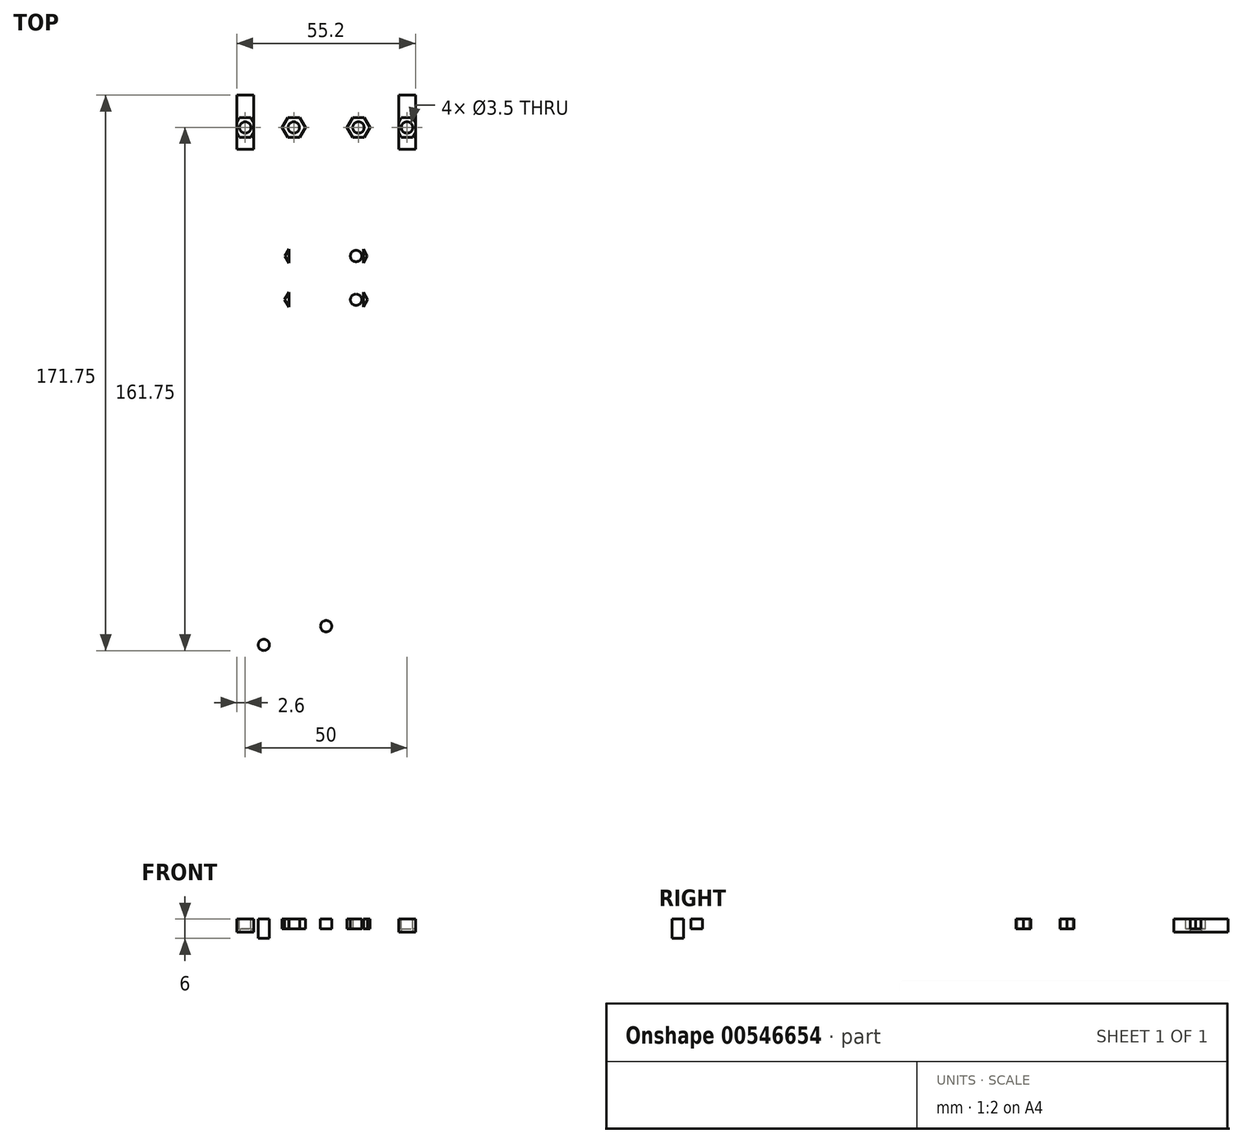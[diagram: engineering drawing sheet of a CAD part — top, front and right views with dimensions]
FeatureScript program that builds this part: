
annotation { "Feature Type Name" : "Feature", "Feature Type Description" : "" }
export const myFeature = defineFeature(function(context is Context, id is Id, definition is map)
    precondition{}
    {
        {
            var Q0;
            Q0=qCreatedBy(makeId("Top.planeOp"),FACE);
            var sketch = newSketch(context, id + "F0", { "sketchPlane" : qUnion([Q0])});
            skLineSegment(sketch, "E0.bottom", {"start": v(45, 105) * mm, "end": v(-45, 105) * mm});
            skLineSegment(sketch, "E0.top", {"start": v(45, -75) * mm, "end": v(-45, -75) * mm});
            skLineSegment(sketch, "E0.left", {"start": v(55, 95) * mm, "end": v(55, -65) * mm});
            skLineSegment(sketch, "E0.right", {"start": v(-55, 95) * mm, "end": v(-55, -65) * mm});
            skLineSegment(sketch, "E1.bottom", {"start": v(55, -3) * mm, "end": v(32, -3) * mm});
            skLineSegment(sketch, "E1.top", {"start": v(55, 77) * mm, "end": v(32, 77) * mm});
            skLineSegment(sketch, "E1.left", {"start": v(55, -3) * mm, "end": v(55, 77) * mm});
            skLineSegment(sketch, "E1.right", {"start": v(32, -3) * mm, "end": v(32, 77) * mm});
            skLineSegment(sketch, "E2.MirrorCS", {"start": v(-32, -3) * mm, "end": v(-32, 77) * mm});
            skLineSegment(sketch, "E3.MirrorCS", {"start": v(-55, 77) * mm, "end": v(-32, 77) * mm});
            skLineSegment(sketch, "E4.MirrorCS", {"start": v(-55, -3) * mm, "end": v(-55, 77) * mm});
            skLineSegment(sketch, "E5.MirrorCS", {"start": v(-55, -3) * mm, "end": v(-32, -3) * mm});
            skPoint(sketch, "E6.visualSharp", {"position": v(-55, 105) * mm});
            skArc(sketch, "E6.filletArc", {"start": v(-45, 105) * mm, "mid": v(-52.07, 102.07) * mm, "end": v(-55, 95) * mm});
            skPoint(sketch, "E7.visualSharp", {"position": v(55, 105) * mm});
            skArc(sketch, "E7.filletArc", {"start": v(55, 95) * mm, "mid": v(52.07, 102.07) * mm, "end": v(45, 105) * mm});
            skPoint(sketch, "E8.visualSharp", {"position": v(55, -75) * mm});
            skArc(sketch, "E8.filletArc", {"start": v(45, -75) * mm, "mid": v(52.07, -72.07) * mm, "end": v(55, -65) * mm});
            skPoint(sketch, "E9.visualSharp", {"position": v(-55, -75) * mm});
            skArc(sketch, "E9.filletArc", {"start": v(-55, -65) * mm, "mid": v(-52.07, -72.07) * mm, "end": v(-45, -75) * mm});
            skLineSegment(sketch, "E10.right", {"start": v(32, 28.9) * mm, "end": v(32, 75.9) * mm});
            skLineSegment(sketch, "E11.bottom", {"start": v(23, 31.6) * mm, "end": v(26, 31.6) * mm});
            skLineSegment(sketch, "E11.top", {"start": v(23, 38.2) * mm, "end": v(26, 38.2) * mm});
            skLineSegment(sketch, "E11.left", {"start": v(23, 31.6) * mm, "end": v(23, 38.2) * mm});
            skLineSegment(sketch, "E11.right", {"start": v(26, 31.6) * mm, "end": v(26, 38.2) * mm});
            skLineSegment(sketch, "E12.bottom", {"start": v(23, 66.6) * mm, "end": v(26, 66.6) * mm});
            skLineSegment(sketch, "E12.top", {"start": v(23, 73.2) * mm, "end": v(26, 73.2) * mm});
            skLineSegment(sketch, "E12.left", {"start": v(23, 66.6) * mm, "end": v(23, 73.2) * mm});
            skLineSegment(sketch, "E12.right", {"start": v(26, 66.6) * mm, "end": v(26, 73.2) * mm});
            skLineSegment(sketch, "E13.bottom", {"start": v(32, 51.9) * mm, "end": v(22, 51.9) * mm});
            skLineSegment(sketch, "E13.top", {"start": v(32, 58.9) * mm, "end": v(22, 58.9) * mm});
            skLineSegment(sketch, "E13.left", {"start": v(32, 51.9) * mm, "end": v(32, 58.9) * mm});
            skLineSegment(sketch, "E13.right", {"start": v(22, 51.9) * mm, "end": v(22, 58.9) * mm});
            skLineSegment(sketch, "E14.MirrorCS", {"start": v(-23, 73.2) * mm, "end": v(-26, 73.2) * mm});
            skLineSegment(sketch, "E15.MirrorCS", {"start": v(-26, 66.6) * mm, "end": v(-26, 73.2) * mm});
            skLineSegment(sketch, "E16.MirrorCS", {"start": v(-23, 66.6) * mm, "end": v(-23, 73.2) * mm});
            skLineSegment(sketch, "E17.MirrorCS", {"start": v(-23, 66.6) * mm, "end": v(-26, 66.6) * mm});
            skLineSegment(sketch, "E18.MirrorCS", {"start": v(-32, 51.9) * mm, "end": v(-32, 58.9) * mm});
            skLineSegment(sketch, "E19.MirrorCS", {"start": v(-32, 58.9) * mm, "end": v(-22, 58.9) * mm});
            skLineSegment(sketch, "E20.MirrorCS", {"start": v(-32, 51.9) * mm, "end": v(-22, 51.9) * mm});
            skLineSegment(sketch, "E21.MirrorCS", {"start": v(-22, 51.9) * mm, "end": v(-22, 58.9) * mm});
            skLineSegment(sketch, "E22.MirrorCS", {"start": v(-23, 38.2) * mm, "end": v(-26, 38.2) * mm});
            skLineSegment(sketch, "E23.MirrorCS", {"start": v(-23, 31.6) * mm, "end": v(-26, 31.6) * mm});
            skLineSegment(sketch, "E24.MirrorCS", {"start": v(-23, 31.6) * mm, "end": v(-23, 38.2) * mm});
            skLineSegment(sketch, "E25.MirrorCS", {"start": v(-26, 31.6) * mm, "end": v(-26, 38.2) * mm});
            skSolve(sketch);
        }
        {
            var Q0;
            Q0=makeQuery(id+"F0.imprint","IMPRINT",FACE,{"disambiguationData":[TD([[makeQuery(id+"F0.imprint","IMPRINT",EDGE,{"derivedFrom":sQuery(id+"F0.wireOp",EDGE,"E0.bottom")}),1.0]])]});
            extrude(context, id + "F1", {"entities" : qUnion([Q0]), "depth" : 6 * mm, "offsetDistance" : 25 * mm});
        }
        {
            var Q0;
            {var subQ0=sQuery(id+"F0.wireOp",EDGE,"E10.right");var subQ1=sQuery(id+"F0.wireOp",EDGE,"E1.right");var subQ2=makeQuery(id+"F0.imprint","INTERSECT",VERTEX,{"disambiguationData":[OD(0.0)],"derivedFrom":[subQ1,subQ0]});Q0=makeQuery(id+"F1.opExtrude","SWEPT_FACE",FACE,{"disambiguationData":[OSD([subQ1,subQ0]),TDD([makeQuery(id+"F0.imprint","IMPRINT",EDGE,{"disambiguationData":[TD([[makeQuery(id+"F0.imprint","INTERSECT",VERTEX,{"derivedFrom":[sQuery(id+"F0.wireOp",EDGE,"E1.bottom"),subQ1]}),-1.0]])],"derivedFrom":subQ1}),makeQuery(id+"F0.imprint","IMPRINT",EDGE,{"disambiguationData":[TD([[subQ2,-1.0]])],"derivedFrom":subQ0})])]});}
            var sketch = newSketch(context, id + "F2", { "sketchPlane" : qUnion([Q0])});
            skCircle(sketch, "E26", {"center": v(34.9, 3) * mm, "radius": 1.75 * mm});
            skCircle(sketch, "E27", {"center": v(69.9, 3) * mm, "radius": 1.75 * mm});
            skSolve(sketch);
        }
        {
            var Q0;
            Q0 = qSketchRegion(id + "F2", true);
            extrude(context, id + "F3", {"entities" : qUnion([Q0]), "operationType" : NewBodyOperationType.REMOVE, "oppositeDirection" : true, "depth" : 15 * mm, "offsetDistance" : 25 * mm});
        }
        {
            var Q0;
            {var subQ0=sQuery(id+"F0.wireOp",EDGE,"E2.MirrorCS");Q0=makeQuery(id+"F1.opExtrude","SWEPT_FACE",FACE,{"disambiguationData":[OSD([subQ0]),TDD([makeQuery(id+"F0.imprint","IMPRINT",EDGE,{"disambiguationData":[TD([[makeQuery(id+"F0.imprint","INTERSECT",VERTEX,{"derivedFrom":[subQ0,sQuery(id+"F0.wireOp",EDGE,"E3.MirrorCS")]}),1.0]])],"derivedFrom":subQ0})])]});}
            var sketch = newSketch(context, id + "F4", { "sketchPlane" : qUnion([Q0])});
            skCircle(sketch, "E28", {"center": v(-69.9, 3) * mm, "radius": 1.75 * mm});
            skCircle(sketch, "E29", {"center": v(-34.9, 3) * mm, "radius": 1.75 * mm});
            skSolve(sketch);
        }
        {
            var Q0;
            Q0=makeQuery(id+"F4.imprint","IMPRINT",FACE,{"disambiguationData":[TD([[makeQuery(id+"F4.imprint","IMPRINT",EDGE,{"derivedFrom":sQuery(id+"F4.wireOp",EDGE,"E28")}),1.0]])]});
            var Q1;
            Q1=makeQuery(id+"F4.imprint","IMPRINT",FACE,{"disambiguationData":[TD([[makeQuery(id+"F4.imprint","IMPRINT",EDGE,{"derivedFrom":sQuery(id+"F4.wireOp",EDGE,"E29")}),1.0]])]});
            extrude(context, id + "F5", {"entities" : qUnion([Q0, Q1]), "operationType" : NewBodyOperationType.REMOVE, "oppositeDirection" : true, "depth" : 15 * mm, "offsetDistance" : 25 * mm});
        }
        {
            var Q0;
            Q0=makeQuery(id+"F1.opExtrude","CAP_FACE",FACE,{"disambiguationData":[OSD([sQuery(id+"F0.wireOp",EDGE,"E0.bottom"),sQuery(id+"F0.wireOp",EDGE,"E0.top"),sQuery(id+"F0.wireOp",EDGE,"E0.left"),sQuery(id+"F0.wireOp",EDGE,"E0.right"),sQuery(id+"F0.wireOp",EDGE,"E1.bottom"),sQuery(id+"F0.wireOp",EDGE,"E1.top"),sQuery(id+"F0.wireOp",EDGE,"E1.right"),sQuery(id+"F0.wireOp",EDGE,"E2.MirrorCS"),sQuery(id+"F0.wireOp",EDGE,"E3.MirrorCS"),sQuery(id+"F0.wireOp",EDGE,"E5.MirrorCS"),sQuery(id+"F0.wireOp",EDGE,"E6.filletArc"),sQuery(id+"F0.wireOp",EDGE,"E7.filletArc"),sQuery(id+"F0.wireOp",EDGE,"E8.filletArc"),sQuery(id+"F0.wireOp",EDGE,"E9.filletArc"),sQuery(id+"F0.wireOp",EDGE,"E10.right"),sQuery(id+"F0.wireOp",EDGE,"E11.bottom"),sQuery(id+"F0.wireOp",EDGE,"E11.top"),sQuery(id+"F0.wireOp",EDGE,"E11.left"),sQuery(id+"F0.wireOp",EDGE,"E11.right"),sQuery(id+"F0.wireOp",EDGE,"E12.bottom"),sQuery(id+"F0.wireOp",EDGE,"E12.top"),sQuery(id+"F0.wireOp",EDGE,"E12.left"),sQuery(id+"F0.wireOp",EDGE,"E12.right"),sQuery(id+"F0.wireOp",EDGE,"E13.bottom"),sQuery(id+"F0.wireOp",EDGE,"E13.top"),sQuery(id+"F0.wireOp",EDGE,"E13.right"),sQuery(id+"F0.wireOp",EDGE,"E14.MirrorCS"),sQuery(id+"F0.wireOp",EDGE,"E15.MirrorCS"),sQuery(id+"F0.wireOp",EDGE,"E16.MirrorCS"),sQuery(id+"F0.wireOp",EDGE,"E17.MirrorCS"),sQuery(id+"F0.wireOp",EDGE,"E19.MirrorCS"),sQuery(id+"F0.wireOp",EDGE,"E20.MirrorCS"),sQuery(id+"F0.wireOp",EDGE,"E21.MirrorCS"),sQuery(id+"F0.wireOp",EDGE,"E22.MirrorCS"),sQuery(id+"F0.wireOp",EDGE,"E23.MirrorCS"),sQuery(id+"F0.wireOp",EDGE,"E24.MirrorCS"),sQuery(id+"F0.wireOp",EDGE,"E25.MirrorCS")])],"isStart":false});
            var sketch = newSketch(context, id + "F6", { "sketchPlane" : qUnion([Q0])});
            skLineSegment(sketch, "E30.bottom", {"start": v(11.5, 61) * mm, "end": v(-11.5, 61) * mm});
            skLineSegment(sketch, "E30.top", {"start": v(11.5, 32) * mm, "end": v(-11.5, 32) * mm});
            skLineSegment(sketch, "E30.left", {"start": v(11.5, 61) * mm, "end": v(11.5, 32) * mm});
            skLineSegment(sketch, "E30.right", {"start": v(-11.5, 61) * mm, "end": v(-11.5, 32) * mm});
            skPoint(sketch, "E30.middle", {"position": v(0, 46.5) * mm});
            skCircle(sketch, "E31", {"center": v(-9.25, 55.25) * mm, "radius": 1.75 * mm});
            skCircle(sketch, "E32.MirrorC", {"center": v(9.25, 55.25) * mm, "radius": 1.75 * mm});
            skCircle(sketch, "E33", {"center": v(-9.25, 41.75) * mm, "radius": 1.75 * mm});
            skCircle(sketch, "E34.MirrorC", {"center": v(9.25, 41.75) * mm, "radius": 1.75 * mm});
            skSolve(sketch);
        }
        {
            var Q0;
            Q0=makeQuery(id+"F6.imprint","IMPRINT",FACE,{"disambiguationData":[TD([[makeQuery(id+"F6.imprint","IMPRINT",EDGE,{"derivedFrom":sQuery(id+"F6.wireOp",EDGE,"E31")}),1.0]])]});
            var Q1;
            Q1=makeQuery(id+"F6.imprint","IMPRINT",FACE,{"disambiguationData":[TD([[makeQuery(id+"F6.imprint","IMPRINT",EDGE,{"derivedFrom":sQuery(id+"F6.wireOp",EDGE,"E32.MirrorC")}),-1.0]])]});
            var Q2;
            Q2=makeQuery(id+"F6.imprint","IMPRINT",FACE,{"disambiguationData":[TD([[makeQuery(id+"F6.imprint","IMPRINT",EDGE,{"derivedFrom":sQuery(id+"F6.wireOp",EDGE,"E34.MirrorC")}),-1.0]])]});
            var Q3;
            Q3=makeQuery(id+"F6.imprint","IMPRINT",FACE,{"disambiguationData":[TD([[makeQuery(id+"F6.imprint","IMPRINT",EDGE,{"derivedFrom":sQuery(id+"F6.wireOp",EDGE,"E33")}),1.0]])]});
            extrude(context, id + "F7", {"entities" : qUnion([Q0, Q1, Q2, Q3]), "operationType" : NewBodyOperationType.REMOVE, "oppositeDirection" : true, "depth" : 25 * mm, "offsetDistance" : 25 * mm});
        }
        {
            var Q0;
            Q0=makeQuery(id+"F1.opExtrude","CAP_FACE",FACE,{"disambiguationData":[OSD([sQuery(id+"F0.wireOp",EDGE,"E0.bottom"),sQuery(id+"F0.wireOp",EDGE,"E0.top"),sQuery(id+"F0.wireOp",EDGE,"E0.left"),sQuery(id+"F0.wireOp",EDGE,"E0.right"),sQuery(id+"F0.wireOp",EDGE,"E1.bottom"),sQuery(id+"F0.wireOp",EDGE,"E1.top"),sQuery(id+"F0.wireOp",EDGE,"E1.right"),sQuery(id+"F0.wireOp",EDGE,"E2.MirrorCS"),sQuery(id+"F0.wireOp",EDGE,"E3.MirrorCS"),sQuery(id+"F0.wireOp",EDGE,"E5.MirrorCS"),sQuery(id+"F0.wireOp",EDGE,"E6.filletArc"),sQuery(id+"F0.wireOp",EDGE,"E7.filletArc"),sQuery(id+"F0.wireOp",EDGE,"E8.filletArc"),sQuery(id+"F0.wireOp",EDGE,"E9.filletArc"),sQuery(id+"F0.wireOp",EDGE,"E10.right"),sQuery(id+"F0.wireOp",EDGE,"E11.bottom"),sQuery(id+"F0.wireOp",EDGE,"E11.top"),sQuery(id+"F0.wireOp",EDGE,"E11.left"),sQuery(id+"F0.wireOp",EDGE,"E11.right"),sQuery(id+"F0.wireOp",EDGE,"E12.bottom"),sQuery(id+"F0.wireOp",EDGE,"E12.top"),sQuery(id+"F0.wireOp",EDGE,"E12.left"),sQuery(id+"F0.wireOp",EDGE,"E12.right"),sQuery(id+"F0.wireOp",EDGE,"E13.bottom"),sQuery(id+"F0.wireOp",EDGE,"E13.top"),sQuery(id+"F0.wireOp",EDGE,"E13.right"),sQuery(id+"F0.wireOp",EDGE,"E14.MirrorCS"),sQuery(id+"F0.wireOp",EDGE,"E15.MirrorCS"),sQuery(id+"F0.wireOp",EDGE,"E16.MirrorCS"),sQuery(id+"F0.wireOp",EDGE,"E17.MirrorCS"),sQuery(id+"F0.wireOp",EDGE,"E19.MirrorCS"),sQuery(id+"F0.wireOp",EDGE,"E20.MirrorCS"),sQuery(id+"F0.wireOp",EDGE,"E21.MirrorCS"),sQuery(id+"F0.wireOp",EDGE,"E22.MirrorCS"),sQuery(id+"F0.wireOp",EDGE,"E23.MirrorCS"),sQuery(id+"F0.wireOp",EDGE,"E24.MirrorCS"),sQuery(id+"F0.wireOp",EDGE,"E25.MirrorCS")])],"isStart":true});
            var sketch = newSketch(context, id + "F8", { "sketchPlane" : qUnion([Q0])});
            skCircle(sketch, "E35.cCircle", {"center": v(-9.25, -41.75) * mm, "radius": 3.1 * mm, "construction": true});
            skLineSegment(sketch, "E35.0", {"start": v(-11.04, -38.65) * mm, "end": v(-7.46, -38.65) * mm});
            skLineSegment(sketch, "E35.1", {"start": v(-7.46, -38.65) * mm, "end": v(-5.67, -41.75) * mm});
            skLineSegment(sketch, "E35.2", {"start": v(-5.67, -41.75) * mm, "end": v(-7.46, -44.85) * mm});
            skLineSegment(sketch, "E35.3", {"start": v(-7.46, -44.85) * mm, "end": v(-11.04, -44.85) * mm});
            skLineSegment(sketch, "E35.4", {"start": v(-11.04, -44.85) * mm, "end": v(-12.83, -41.75) * mm});
            skLineSegment(sketch, "E35.5", {"start": v(-12.83, -41.75) * mm, "end": v(-11.04, -38.65) * mm});
            skPoint(sketch, "E35.0.midPoint", {"position": v(-9.25, -38.65) * mm});
            skCircle(sketch, "E36.MirrorC", {"center": v(9.25, -41.75) * mm, "radius": 3.1 * mm, "construction": true});
            skLineSegment(sketch, "E37.MirrorCS", {"start": v(5.67, -41.75) * mm, "end": v(7.46, -44.85) * mm});
            skLineSegment(sketch, "E38.MirrorCS", {"start": v(7.46, -38.65) * mm, "end": v(5.67, -41.75) * mm});
            skLineSegment(sketch, "E39.MirrorCS", {"start": v(11.04, -38.65) * mm, "end": v(7.46, -38.65) * mm});
            skPoint(sketch, "E40.MirrorP", {"position": v(9.25, -38.65) * mm});
            skLineSegment(sketch, "E41.MirrorCS", {"start": v(7.46, -44.85) * mm, "end": v(11.04, -44.85) * mm});
            skLineSegment(sketch, "E42.MirrorCS", {"start": v(11.04, -44.85) * mm, "end": v(12.83, -41.75) * mm});
            skLineSegment(sketch, "E43.MirrorCS", {"start": v(12.83, -41.75) * mm, "end": v(11.04, -38.65) * mm});
            skCircle(sketch, "E44.cCircle", {"center": v(-9.25, -55.25) * mm, "radius": 3 * mm, "construction": true});
            skLineSegment(sketch, "E44.0", {"start": v(-10.98, -52.25) * mm, "end": v(-7.52, -52.25) * mm});
            skLineSegment(sketch, "E44.1", {"start": v(-7.52, -52.25) * mm, "end": v(-5.79, -55.25) * mm});
            skLineSegment(sketch, "E44.2", {"start": v(-5.79, -55.25) * mm, "end": v(-7.52, -58.25) * mm});
            skLineSegment(sketch, "E44.3", {"start": v(-7.52, -58.25) * mm, "end": v(-10.98, -58.25) * mm});
            skLineSegment(sketch, "E44.4", {"start": v(-10.98, -58.25) * mm, "end": v(-12.71, -55.25) * mm});
            skLineSegment(sketch, "E44.5", {"start": v(-12.71, -55.25) * mm, "end": v(-10.98, -52.25) * mm});
            skPoint(sketch, "E44.0.midPoint", {"position": v(-9.25, -52.25) * mm});
            skCircle(sketch, "E45.MirrorC", {"center": v(9.25, -55.25) * mm, "radius": 3 * mm, "construction": true});
            skLineSegment(sketch, "E46.MirrorCS", {"start": v(5.79, -55.25) * mm, "end": v(7.52, -58.25) * mm});
            skLineSegment(sketch, "E47.MirrorCS", {"start": v(7.52, -52.25) * mm, "end": v(5.79, -55.25) * mm});
            skLineSegment(sketch, "E48.MirrorCS", {"start": v(10.98, -52.25) * mm, "end": v(7.52, -52.25) * mm});
            skPoint(sketch, "E49.MirrorP", {"position": v(9.25, -52.25) * mm});
            skLineSegment(sketch, "E50.MirrorCS", {"start": v(7.52, -58.25) * mm, "end": v(10.98, -58.25) * mm});
            skLineSegment(sketch, "E51.MirrorCS", {"start": v(12.71, -55.25) * mm, "end": v(10.98, -52.25) * mm});
            skLineSegment(sketch, "E52.MirrorCS", {"start": v(10.98, -58.25) * mm, "end": v(12.71, -55.25) * mm});
            skSolve(sketch);
        }
        {
            var Q0;
            Q0 = qSketchRegion(id + "F8", true);
            extrude(context, id + "F9", {"entities" : qUnion([Q0]), "operationType" : NewBodyOperationType.REMOVE, "oppositeDirection" : true, "depth" : 3 * mm, "offsetDistance" : 25 * mm});
        }
        {
            var Q0;
            Q0=makeQuery(id+"F1.opExtrude","CAP_FACE",FACE,{"disambiguationData":[OSD([sQuery(id+"F0.wireOp",EDGE,"E0.bottom"),sQuery(id+"F0.wireOp",EDGE,"E0.top"),sQuery(id+"F0.wireOp",EDGE,"E0.left"),sQuery(id+"F0.wireOp",EDGE,"E0.right"),sQuery(id+"F0.wireOp",EDGE,"E1.bottom"),sQuery(id+"F0.wireOp",EDGE,"E1.top"),sQuery(id+"F0.wireOp",EDGE,"E1.right"),sQuery(id+"F0.wireOp",EDGE,"E2.MirrorCS"),sQuery(id+"F0.wireOp",EDGE,"E3.MirrorCS"),sQuery(id+"F0.wireOp",EDGE,"E5.MirrorCS"),sQuery(id+"F0.wireOp",EDGE,"E6.filletArc"),sQuery(id+"F0.wireOp",EDGE,"E7.filletArc"),sQuery(id+"F0.wireOp",EDGE,"E8.filletArc"),sQuery(id+"F0.wireOp",EDGE,"E9.filletArc"),sQuery(id+"F0.wireOp",EDGE,"E10.right"),sQuery(id+"F0.wireOp",EDGE,"E11.bottom"),sQuery(id+"F0.wireOp",EDGE,"E11.top"),sQuery(id+"F0.wireOp",EDGE,"E11.left"),sQuery(id+"F0.wireOp",EDGE,"E11.right"),sQuery(id+"F0.wireOp",EDGE,"E12.bottom"),sQuery(id+"F0.wireOp",EDGE,"E12.top"),sQuery(id+"F0.wireOp",EDGE,"E12.left"),sQuery(id+"F0.wireOp",EDGE,"E12.right"),sQuery(id+"F0.wireOp",EDGE,"E13.bottom"),sQuery(id+"F0.wireOp",EDGE,"E13.top"),sQuery(id+"F0.wireOp",EDGE,"E13.right"),sQuery(id+"F0.wireOp",EDGE,"E14.MirrorCS"),sQuery(id+"F0.wireOp",EDGE,"E15.MirrorCS"),sQuery(id+"F0.wireOp",EDGE,"E16.MirrorCS"),sQuery(id+"F0.wireOp",EDGE,"E17.MirrorCS"),sQuery(id+"F0.wireOp",EDGE,"E19.MirrorCS"),sQuery(id+"F0.wireOp",EDGE,"E20.MirrorCS"),sQuery(id+"F0.wireOp",EDGE,"E21.MirrorCS"),sQuery(id+"F0.wireOp",EDGE,"E22.MirrorCS"),sQuery(id+"F0.wireOp",EDGE,"E23.MirrorCS"),sQuery(id+"F0.wireOp",EDGE,"E24.MirrorCS"),sQuery(id+"F0.wireOp",EDGE,"E25.MirrorCS")])],"isStart":false});
            var sketch = newSketch(context, id + "F10", { "sketchPlane" : qUnion([Q0])});
            skLineSegment(sketch, "E53.bottom", {"start": v(-55, -13) * mm, "end": v(55, -13) * mm});
            skLineSegment(sketch, "E53.top", {"start": v(-55, -55) * mm, "end": v(55, -55) * mm});
            skLineSegment(sketch, "E53.left", {"start": v(-55, -13) * mm, "end": v(-55, -55) * mm});
            skLineSegment(sketch, "E53.right", {"start": v(55, -13) * mm, "end": v(55, -55) * mm});
            skLineSegment(sketch, "E54.bottom", {"start": v(-4.2, -4.6) * mm, "end": v(4.2, -4.6) * mm});
            skLineSegment(sketch, "E54.top", {"start": v(-4.2, -13) * mm, "end": v(4.2, -13) * mm});
            skLineSegment(sketch, "E54.left", {"start": v(-4.2, -4.6) * mm, "end": v(-4.2, -13) * mm});
            skLineSegment(sketch, "E54.right", {"start": v(4.2, -4.6) * mm, "end": v(4.2, -13) * mm});
            skLineSegment(sketch, "E55.MirrorCS", {"start": v(-4.2, -55) * mm, "end": v(4.2, -55) * mm});
            skLineSegment(sketch, "E56.MirrorCS", {"start": v(-4.2, -63.4) * mm, "end": v(-4.2, -55) * mm});
            skLineSegment(sketch, "E57.MirrorCS", {"start": v(4.2, -63.4) * mm, "end": v(4.2, -55) * mm});
            skLineSegment(sketch, "E58.MirrorCS", {"start": v(-4.2, -63.4) * mm, "end": v(4.2, -63.4) * mm});
            skSolve(sketch);
        }
        {
            var Q0;
            Q0=makeQuery(id+"F10.imprint","IMPRINT",FACE,{"disambiguationData":[TD([[makeQuery(id+"F10.imprint","IMPRINT",EDGE,{"derivedFrom":sQuery(id+"F10.wireOp",EDGE,"c6e326e5-0ca1-43d0-984c-ec21a27a9c8d0.MirrorCS")}),1.0]])]});
            var Q1;
            Q1=makeQuery(id+"F10.imprint","IMPRINT",FACE,{"disambiguationData":[TD([[makeQuery(id+"F10.imprint","IMPRINT",EDGE,{"derivedFrom":sQuery(id+"F10.wireOp",EDGE,"E55.MirrorCS")}),-1.0]])]});
            var Q2;
            Q2=makeQuery(id+"F10.imprint","IMPRINT",FACE,{"disambiguationData":[TD([[makeQuery(id+"F10.imprint","IMPRINT",EDGE,{"derivedFrom":sQuery(id+"F10.wireOp",EDGE,"450c8181-7459-44c8-8380-1bca4ead6bea2.MirrorCS")}),-1.0]])]});
            var Q3;
            Q3=makeQuery(id+"F10.imprint","IMPRINT",FACE,{"disambiguationData":[TD([[makeQuery(id+"F10.imprint","IMPRINT",EDGE,{"derivedFrom":sQuery(id+"F10.wireOp",EDGE,"E54.bottom")}),-1.0]])]});
            extrude(context, id + "F11", {"entities" : qUnion([Q0, Q1, Q2, Q3]), "operationType" : NewBodyOperationType.REMOVE, "oppositeDirection" : true, "depth" : 3 * mm, "offsetDistance" : 25 * mm});
        }
        {
            var Q0;
            {var subQ2=sQuery(id+"F10.wireOp",EDGE,"E53.left");Q0=makeQuery(id+"F10.imprint","IMPRINT",FACE,{"disambiguationData":[TD([[makeQuery(id+"F10.imprint","IMPRINT",EDGE,{"derivedFrom":subQ2}),1.0]])]});}
            extrude(context, id + "F12", {"entities" : qUnion([Q0]), "operationType" : NewBodyOperationType.REMOVE, "oppositeDirection" : true, "depth" : 2 * mm, "offsetDistance" : 25 * mm});
        }
        {
            var Q0;
            Q0=makeQuery(id+"F11.boolean.opBoolean","COPY",FACE,{"derivedFrom":makeQuery(id+"F11.opExtrude","CAP_FACE",FACE,{"disambiguationData":[OSD([sQuery(id+"F10.wireOp",EDGE,"E54.bottom"),sQuery(id+"F10.wireOp",EDGE,"E54.top"),sQuery(id+"F10.wireOp",EDGE,"E54.left"),sQuery(id+"F10.wireOp",EDGE,"E54.right")])],"isStart":false})});
            var sketch = newSketch(context, id + "F13", { "sketchPlane" : qUnion([Q0])});
            skCircle(sketch, "E59", {"center": v(0, -8.8) * mm, "radius": 1.75 * mm});
            skCircle(sketch, "E60", {"center": v(0, -59.2) * mm, "radius": 1.75 * mm});
            skSolve(sketch);
        }
        {
            var Q0;
            Q0 = qSketchRegion(id + "F13", true);
            extrude(context, id + "F14", {"entities" : qUnion([Q0]), "operationType" : NewBodyOperationType.REMOVE, "oppositeDirection" : true, "depth" : 25 * mm, "offsetDistance" : 25 * mm});
        }
        {
            var Q0;
            {var subQ0=sQuery(id+"F0.wireOp",EDGE,"E12.left");var subQ1=sQuery(id+"F0.wireOp",EDGE,"E12.top");var subQ2=sQuery(id+"F0.wireOp",EDGE,"E12.bottom");var subQ3=sQuery(id+"F0.wireOp",EDGE,"E11.left");var subQ4=sQuery(id+"F0.wireOp",EDGE,"E11.top");var subQ5=sQuery(id+"F0.wireOp",EDGE,"E11.bottom");var subQ6=sQuery(id+"F0.wireOp",EDGE,"E7.filletArc");var subQ7=sQuery(id+"F0.wireOp",EDGE,"E6.filletArc");var subQ8=sQuery(id+"F0.wireOp",EDGE,"E5.MirrorCS");var subQ9=sQuery(id+"F0.wireOp",EDGE,"E3.MirrorCS");var subQ10=sQuery(id+"F0.wireOp",EDGE,"E2.MirrorCS");var subQ11=sQuery(id+"F0.wireOp",EDGE,"E19.MirrorCS");var subQ13=sQuery(id+"F0.wireOp",EDGE,"E0.right");var subQ15=sQuery(id+"F0.wireOp",EDGE,"E0.left");var subQ17=sQuery(id+"F0.wireOp",EDGE,"E1.top");var subQ18=sQuery(id+"F0.wireOp",EDGE,"E8.filletArc");var subQ19=sQuery(id+"F0.wireOp",EDGE,"E1.bottom");var subQ20=sQuery(id+"F0.wireOp",EDGE,"E11.right");var subQ21=sQuery(id+"F0.wireOp",EDGE,"E0.bottom");var subQ22=sQuery(id+"F0.wireOp",EDGE,"E10.right");var subQ23=sQuery(id+"F0.wireOp",EDGE,"E1.right");var subQ26=sQuery(id+"F0.wireOp",EDGE,"E13.top");var subQ27=sQuery(id+"F0.wireOp",EDGE,"E9.filletArc");var subQ29=sQuery(id+"F0.wireOp",EDGE,"E13.bottom");var subQ30=sQuery(id+"F0.wireOp",EDGE,"E20.MirrorCS");var subQ31=sQuery(id+"F0.wireOp",EDGE,"E12.right");var subQ32=sQuery(id+"F0.wireOp",EDGE,"E13.right");var subQ33=sQuery(id+"F0.wireOp",EDGE,"E14.MirrorCS");var subQ34=sQuery(id+"F0.wireOp",EDGE,"E15.MirrorCS");var subQ35=sQuery(id+"F0.wireOp",EDGE,"E16.MirrorCS");var subQ36=sQuery(id+"F0.wireOp",EDGE,"E17.MirrorCS");var subQ37=sQuery(id+"F0.wireOp",EDGE,"E21.MirrorCS");var subQ38=sQuery(id+"F0.wireOp",EDGE,"E22.MirrorCS");var subQ39=sQuery(id+"F0.wireOp",EDGE,"E23.MirrorCS");var subQ40=sQuery(id+"F0.wireOp",EDGE,"E24.MirrorCS");var subQ41=sQuery(id+"F0.wireOp",EDGE,"E25.MirrorCS");Q0=makeQuery(id+"F12.boolean.opBoolean","SPLIT",FACE,{"disambiguationData":[TD([makeQuery(id+"F1.opExtrude","SWEPT_FACE",FACE,{"disambiguationData":[OSD([subQ21])]})])],"derivedFrom":makeQuery(id+"F1.opExtrude","CAP_FACE",FACE,{"disambiguationData":[OSD([subQ21,sQuery(id+"F0.wireOp",EDGE,"E0.top"),subQ15,subQ13,subQ19,subQ17,subQ23,subQ10,subQ9,subQ8,subQ7,subQ6,subQ18,subQ27,subQ22,subQ5,subQ4,subQ3,subQ20,subQ2,subQ1,subQ0,subQ31,subQ29,subQ26,subQ32,subQ33,subQ34,subQ35,subQ36,subQ11,subQ30,subQ37,subQ38,subQ39,subQ40,subQ41])],"isStart":false})});}
            var sketch = newSketch(context, id + "F15", { "sketchPlane" : qUnion([Q0])});
            skCircle(sketch, "E61", {"center": v(-45, 95) * mm, "radius": 1.75 * mm});
            skCircle(sketch, "E62.MirrorC", {"center": v(45, 95) * mm, "radius": 1.75 * mm});
            skCircle(sketch, "E63", {"center": v(45, -65) * mm, "radius": 1.75 * mm});
            skCircle(sketch, "E64.MirrorC", {"center": v(-45, -65) * mm, "radius": 1.75 * mm});
            skSolve(sketch);
        }
        {
            var Q0;
            Q0 = qSketchRegion(id + "F15", true);
            extrude(context, id + "F16", {"entities" : qUnion([Q0]), "operationType" : NewBodyOperationType.REMOVE, "oppositeDirection" : true, "depth" : 25 * mm, "offsetDistance" : 25 * mm});
        }
        {
            var Q0;
            Q0=makeQuery(id+"F1.opExtrude","CAP_FACE",FACE,{"disambiguationData":[OSD([sQuery(id+"F0.wireOp",EDGE,"E0.bottom"),sQuery(id+"F0.wireOp",EDGE,"E0.top"),sQuery(id+"F0.wireOp",EDGE,"E0.left"),sQuery(id+"F0.wireOp",EDGE,"E0.right"),sQuery(id+"F0.wireOp",EDGE,"E1.bottom"),sQuery(id+"F0.wireOp",EDGE,"E1.top"),sQuery(id+"F0.wireOp",EDGE,"E1.right"),sQuery(id+"F0.wireOp",EDGE,"E2.MirrorCS"),sQuery(id+"F0.wireOp",EDGE,"E3.MirrorCS"),sQuery(id+"F0.wireOp",EDGE,"E5.MirrorCS"),sQuery(id+"F0.wireOp",EDGE,"E6.filletArc"),sQuery(id+"F0.wireOp",EDGE,"E7.filletArc"),sQuery(id+"F0.wireOp",EDGE,"E8.filletArc"),sQuery(id+"F0.wireOp",EDGE,"E9.filletArc"),sQuery(id+"F0.wireOp",EDGE,"E10.right"),sQuery(id+"F0.wireOp",EDGE,"E11.bottom"),sQuery(id+"F0.wireOp",EDGE,"E11.top"),sQuery(id+"F0.wireOp",EDGE,"E11.left"),sQuery(id+"F0.wireOp",EDGE,"E11.right"),sQuery(id+"F0.wireOp",EDGE,"E12.bottom"),sQuery(id+"F0.wireOp",EDGE,"E12.top"),sQuery(id+"F0.wireOp",EDGE,"E12.left"),sQuery(id+"F0.wireOp",EDGE,"E12.right"),sQuery(id+"F0.wireOp",EDGE,"E13.bottom"),sQuery(id+"F0.wireOp",EDGE,"E13.top"),sQuery(id+"F0.wireOp",EDGE,"E13.right"),sQuery(id+"F0.wireOp",EDGE,"E14.MirrorCS"),sQuery(id+"F0.wireOp",EDGE,"E15.MirrorCS"),sQuery(id+"F0.wireOp",EDGE,"E16.MirrorCS"),sQuery(id+"F0.wireOp",EDGE,"E17.MirrorCS"),sQuery(id+"F0.wireOp",EDGE,"E19.MirrorCS"),sQuery(id+"F0.wireOp",EDGE,"E20.MirrorCS"),sQuery(id+"F0.wireOp",EDGE,"E21.MirrorCS"),sQuery(id+"F0.wireOp",EDGE,"E22.MirrorCS"),sQuery(id+"F0.wireOp",EDGE,"E23.MirrorCS"),sQuery(id+"F0.wireOp",EDGE,"E24.MirrorCS"),sQuery(id+"F0.wireOp",EDGE,"E25.MirrorCS")])],"isStart":true});
            var sketch = newSketch(context, id + "F17", { "sketchPlane" : qUnion([Q0])});
            skCircle(sketch, "E65", {"center": v(-25, -95) * mm, "radius": 1.75 * mm});
            skCircle(sketch, "E66.MirrorC", {"center": v(25, -95) * mm, "radius": 1.75 * mm});
            skSolve(sketch);
        }
        {
            var Q0;
            Q0 = qSketchRegion(id + "F17", true);
            extrude(context, id + "F18", {"entities" : qUnion([Q0]), "operationType" : NewBodyOperationType.REMOVE, "oppositeDirection" : true, "depth" : 25 * mm, "offsetDistance" : 25 * mm});
        }
        {
            var Q0;
            {var subQ0=sQuery(id+"F0.wireOp",EDGE,"E12.left");var subQ1=sQuery(id+"F0.wireOp",EDGE,"E12.top");var subQ2=sQuery(id+"F0.wireOp",EDGE,"E12.bottom");var subQ3=sQuery(id+"F0.wireOp",EDGE,"E11.left");var subQ4=sQuery(id+"F0.wireOp",EDGE,"E11.top");var subQ5=sQuery(id+"F0.wireOp",EDGE,"E11.bottom");var subQ6=sQuery(id+"F0.wireOp",EDGE,"E7.filletArc");var subQ7=sQuery(id+"F0.wireOp",EDGE,"E6.filletArc");var subQ8=sQuery(id+"F0.wireOp",EDGE,"E5.MirrorCS");var subQ9=sQuery(id+"F0.wireOp",EDGE,"E3.MirrorCS");var subQ10=sQuery(id+"F0.wireOp",EDGE,"E2.MirrorCS");var subQ11=sQuery(id+"F0.wireOp",EDGE,"E19.MirrorCS");var subQ13=sQuery(id+"F0.wireOp",EDGE,"E0.right");var subQ15=sQuery(id+"F0.wireOp",EDGE,"E0.left");var subQ17=sQuery(id+"F0.wireOp",EDGE,"E1.top");var subQ18=sQuery(id+"F0.wireOp",EDGE,"E8.filletArc");var subQ19=sQuery(id+"F0.wireOp",EDGE,"E1.bottom");var subQ20=sQuery(id+"F0.wireOp",EDGE,"E11.right");var subQ21=sQuery(id+"F0.wireOp",EDGE,"E0.bottom");var subQ22=sQuery(id+"F0.wireOp",EDGE,"E10.right");var subQ23=sQuery(id+"F0.wireOp",EDGE,"E1.right");var subQ26=sQuery(id+"F0.wireOp",EDGE,"E13.top");var subQ27=sQuery(id+"F0.wireOp",EDGE,"E9.filletArc");var subQ29=sQuery(id+"F0.wireOp",EDGE,"E13.bottom");var subQ30=sQuery(id+"F0.wireOp",EDGE,"E20.MirrorCS");var subQ31=sQuery(id+"F0.wireOp",EDGE,"E12.right");var subQ32=sQuery(id+"F0.wireOp",EDGE,"E13.right");var subQ33=sQuery(id+"F0.wireOp",EDGE,"E14.MirrorCS");var subQ34=sQuery(id+"F0.wireOp",EDGE,"E15.MirrorCS");var subQ35=sQuery(id+"F0.wireOp",EDGE,"E16.MirrorCS");var subQ36=sQuery(id+"F0.wireOp",EDGE,"E17.MirrorCS");var subQ37=sQuery(id+"F0.wireOp",EDGE,"E21.MirrorCS");var subQ38=sQuery(id+"F0.wireOp",EDGE,"E22.MirrorCS");var subQ39=sQuery(id+"F0.wireOp",EDGE,"E23.MirrorCS");var subQ40=sQuery(id+"F0.wireOp",EDGE,"E24.MirrorCS");var subQ41=sQuery(id+"F0.wireOp",EDGE,"E25.MirrorCS");Q0=makeQuery(id+"F12.boolean.opBoolean","SPLIT",FACE,{"disambiguationData":[TD([makeQuery(id+"F1.opExtrude","SWEPT_FACE",FACE,{"disambiguationData":[OSD([subQ21])]})])],"derivedFrom":makeQuery(id+"F1.opExtrude","CAP_FACE",FACE,{"disambiguationData":[OSD([subQ21,sQuery(id+"F0.wireOp",EDGE,"E0.top"),subQ15,subQ13,subQ19,subQ17,subQ23,subQ10,subQ9,subQ8,subQ7,subQ6,subQ18,subQ27,subQ22,subQ5,subQ4,subQ3,subQ20,subQ2,subQ1,subQ0,subQ31,subQ29,subQ26,subQ32,subQ33,subQ34,subQ35,subQ36,subQ11,subQ30,subQ37,subQ38,subQ39,subQ40,subQ41])],"isStart":false})});}
            var sketch = newSketch(context, id + "F19", { "sketchPlane" : qUnion([Q0])});
            skCircle(sketch, "E67.cCircle", {"center": v(-25, 95) * mm, "radius": 3.1 * mm, "construction": true});
            skLineSegment(sketch, "E67.0", {"start": v(-26.79, 98.1) * mm, "end": v(-23.21, 98.1) * mm});
            skLineSegment(sketch, "E67.1", {"start": v(-23.21, 98.1) * mm, "end": v(-21.42, 95) * mm});
            skLineSegment(sketch, "E67.2", {"start": v(-21.42, 95) * mm, "end": v(-23.21, 91.9) * mm});
            skLineSegment(sketch, "E67.3", {"start": v(-23.21, 91.9) * mm, "end": v(-26.79, 91.9) * mm});
            skLineSegment(sketch, "E67.4", {"start": v(-26.79, 91.9) * mm, "end": v(-28.58, 95) * mm});
            skLineSegment(sketch, "E67.5", {"start": v(-28.58, 95) * mm, "end": v(-26.79, 98.1) * mm});
            skPoint(sketch, "E67.0.midPoint", {"position": v(-25, 98.1) * mm});
            skLineSegment(sketch, "E68.MirrorCS", {"start": v(26.79, 91.9) * mm, "end": v(28.58, 95) * mm});
            skLineSegment(sketch, "E69.MirrorCS", {"start": v(23.21, 98.1) * mm, "end": v(21.42, 95) * mm});
            skLineSegment(sketch, "E70.MirrorCS", {"start": v(23.21, 91.9) * mm, "end": v(26.79, 91.9) * mm});
            skPoint(sketch, "E71.MirrorP", {"position": v(25, 98.1) * mm});
            skLineSegment(sketch, "E72.MirrorCS", {"start": v(21.42, 95) * mm, "end": v(23.21, 91.9) * mm});
            skLineSegment(sketch, "E73.MirrorCS", {"start": v(26.79, 98.1) * mm, "end": v(23.21, 98.1) * mm});
            skCircle(sketch, "E74.MirrorC", {"center": v(25, 95) * mm, "radius": 3.1 * mm, "construction": true});
            skLineSegment(sketch, "E75.MirrorCS", {"start": v(28.58, 95) * mm, "end": v(26.79, 98.1) * mm});
            skSolve(sketch);
        }
        {
            var Q0;
            Q0 = qSketchRegion(id + "F19", true);
            extrude(context, id + "F20", {"entities" : qUnion([Q0]), "operationType" : NewBodyOperationType.REMOVE, "oppositeDirection" : true, "depth" : 3 * mm, "offsetDistance" : 25 * mm});
        }
        {
            var Q0;
            Q0=makeQuery(id+"F1.opExtrude","CAP_FACE",FACE,{"disambiguationData":[OSD([sQuery(id+"F0.wireOp",EDGE,"E0.bottom"),sQuery(id+"F0.wireOp",EDGE,"E0.top"),sQuery(id+"F0.wireOp",EDGE,"E0.left"),sQuery(id+"F0.wireOp",EDGE,"E0.right"),sQuery(id+"F0.wireOp",EDGE,"E1.bottom"),sQuery(id+"F0.wireOp",EDGE,"E1.top"),sQuery(id+"F0.wireOp",EDGE,"E1.right"),sQuery(id+"F0.wireOp",EDGE,"E2.MirrorCS"),sQuery(id+"F0.wireOp",EDGE,"E3.MirrorCS"),sQuery(id+"F0.wireOp",EDGE,"E5.MirrorCS"),sQuery(id+"F0.wireOp",EDGE,"E6.filletArc"),sQuery(id+"F0.wireOp",EDGE,"E7.filletArc"),sQuery(id+"F0.wireOp",EDGE,"E8.filletArc"),sQuery(id+"F0.wireOp",EDGE,"E9.filletArc"),sQuery(id+"F0.wireOp",EDGE,"E10.right"),sQuery(id+"F0.wireOp",EDGE,"E11.bottom"),sQuery(id+"F0.wireOp",EDGE,"E11.top"),sQuery(id+"F0.wireOp",EDGE,"E11.left"),sQuery(id+"F0.wireOp",EDGE,"E11.right"),sQuery(id+"F0.wireOp",EDGE,"E12.bottom"),sQuery(id+"F0.wireOp",EDGE,"E12.top"),sQuery(id+"F0.wireOp",EDGE,"E12.left"),sQuery(id+"F0.wireOp",EDGE,"E12.right"),sQuery(id+"F0.wireOp",EDGE,"E13.bottom"),sQuery(id+"F0.wireOp",EDGE,"E13.top"),sQuery(id+"F0.wireOp",EDGE,"E13.right"),sQuery(id+"F0.wireOp",EDGE,"E14.MirrorCS"),sQuery(id+"F0.wireOp",EDGE,"E15.MirrorCS"),sQuery(id+"F0.wireOp",EDGE,"E16.MirrorCS"),sQuery(id+"F0.wireOp",EDGE,"E17.MirrorCS"),sQuery(id+"F0.wireOp",EDGE,"E19.MirrorCS"),sQuery(id+"F0.wireOp",EDGE,"E20.MirrorCS"),sQuery(id+"F0.wireOp",EDGE,"E21.MirrorCS"),sQuery(id+"F0.wireOp",EDGE,"E22.MirrorCS"),sQuery(id+"F0.wireOp",EDGE,"E23.MirrorCS"),sQuery(id+"F0.wireOp",EDGE,"E24.MirrorCS"),sQuery(id+"F0.wireOp",EDGE,"E25.MirrorCS")])],"isStart":true});
            var sketch = newSketch(context, id + "F21", { "sketchPlane" : qUnion([Q0])});
            skCircle(sketch, "E76", {"center": v(-10, -95) * mm, "radius": 1.75 * mm});
            skCircle(sketch, "E77.MirrorC", {"center": v(10, -95) * mm, "radius": 1.75 * mm});
            skSolve(sketch);
        }
        {
            var Q0;
            Q0 = qSketchRegion(id + "F21", true);
            extrude(context, id + "F22", {"entities" : qUnion([Q0]), "operationType" : NewBodyOperationType.REMOVE, "oppositeDirection" : true, "depth" : 25 * mm, "offsetDistance" : 25 * mm});
        }
        {
            var Q0;
            Q0=makeQuery(id+"F1.opExtrude","CAP_FACE",FACE,{"disambiguationData":[OSD([sQuery(id+"F0.wireOp",EDGE,"E0.bottom"),sQuery(id+"F0.wireOp",EDGE,"E0.top"),sQuery(id+"F0.wireOp",EDGE,"E0.left"),sQuery(id+"F0.wireOp",EDGE,"E0.right"),sQuery(id+"F0.wireOp",EDGE,"E1.bottom"),sQuery(id+"F0.wireOp",EDGE,"E1.top"),sQuery(id+"F0.wireOp",EDGE,"E1.right"),sQuery(id+"F0.wireOp",EDGE,"E2.MirrorCS"),sQuery(id+"F0.wireOp",EDGE,"E3.MirrorCS"),sQuery(id+"F0.wireOp",EDGE,"E5.MirrorCS"),sQuery(id+"F0.wireOp",EDGE,"E6.filletArc"),sQuery(id+"F0.wireOp",EDGE,"E7.filletArc"),sQuery(id+"F0.wireOp",EDGE,"E8.filletArc"),sQuery(id+"F0.wireOp",EDGE,"E9.filletArc"),sQuery(id+"F0.wireOp",EDGE,"E10.right"),sQuery(id+"F0.wireOp",EDGE,"E11.bottom"),sQuery(id+"F0.wireOp",EDGE,"E11.top"),sQuery(id+"F0.wireOp",EDGE,"E11.left"),sQuery(id+"F0.wireOp",EDGE,"E11.right"),sQuery(id+"F0.wireOp",EDGE,"E12.bottom"),sQuery(id+"F0.wireOp",EDGE,"E12.top"),sQuery(id+"F0.wireOp",EDGE,"E12.left"),sQuery(id+"F0.wireOp",EDGE,"E12.right"),sQuery(id+"F0.wireOp",EDGE,"E13.bottom"),sQuery(id+"F0.wireOp",EDGE,"E13.top"),sQuery(id+"F0.wireOp",EDGE,"E13.right"),sQuery(id+"F0.wireOp",EDGE,"E14.MirrorCS"),sQuery(id+"F0.wireOp",EDGE,"E15.MirrorCS"),sQuery(id+"F0.wireOp",EDGE,"E16.MirrorCS"),sQuery(id+"F0.wireOp",EDGE,"E17.MirrorCS"),sQuery(id+"F0.wireOp",EDGE,"E19.MirrorCS"),sQuery(id+"F0.wireOp",EDGE,"E20.MirrorCS"),sQuery(id+"F0.wireOp",EDGE,"E21.MirrorCS"),sQuery(id+"F0.wireOp",EDGE,"E22.MirrorCS"),sQuery(id+"F0.wireOp",EDGE,"E23.MirrorCS"),sQuery(id+"F0.wireOp",EDGE,"E24.MirrorCS"),sQuery(id+"F0.wireOp",EDGE,"E25.MirrorCS")])],"isStart":true});
            var sketch = newSketch(context, id + "F23", { "sketchPlane" : qUnion([Q0])});
            skCircle(sketch, "E78.cCircle", {"center": v(-10, -95) * mm, "radius": 3.1 * mm, "construction": true});
            skLineSegment(sketch, "E78.0", {"start": v(-11.79, -91.9) * mm, "end": v(-8.21, -91.9) * mm});
            skLineSegment(sketch, "E78.1", {"start": v(-8.21, -91.9) * mm, "end": v(-6.42, -95) * mm});
            skLineSegment(sketch, "E78.2", {"start": v(-6.42, -95) * mm, "end": v(-8.21, -98.1) * mm});
            skLineSegment(sketch, "E78.3", {"start": v(-8.21, -98.1) * mm, "end": v(-11.79, -98.1) * mm});
            skLineSegment(sketch, "E78.4", {"start": v(-11.79, -98.1) * mm, "end": v(-13.58, -95) * mm});
            skLineSegment(sketch, "E78.5", {"start": v(-13.58, -95) * mm, "end": v(-11.79, -91.9) * mm});
            skPoint(sketch, "E78.0.midPoint", {"position": v(-10, -91.9) * mm});
            skLineSegment(sketch, "E79.MirrorCS", {"start": v(11.79, -91.9) * mm, "end": v(8.21, -91.9) * mm});
            skLineSegment(sketch, "E80.MirrorCS", {"start": v(8.21, -91.9) * mm, "end": v(6.42, -95) * mm});
            skPoint(sketch, "E81.MirrorP", {"position": v(10, -91.9) * mm});
            skLineSegment(sketch, "E82.MirrorCS", {"start": v(6.42, -95) * mm, "end": v(8.21, -98.1) * mm});
            skLineSegment(sketch, "E83.MirrorCS", {"start": v(8.21, -98.1) * mm, "end": v(11.79, -98.1) * mm});
            skCircle(sketch, "E84.MirrorC", {"center": v(10, -95) * mm, "radius": 3.1 * mm, "construction": true});
            skLineSegment(sketch, "E85.MirrorCS", {"start": v(11.79, -98.1) * mm, "end": v(13.58, -95) * mm});
            skLineSegment(sketch, "E86.MirrorCS", {"start": v(13.58, -95) * mm, "end": v(11.79, -91.9) * mm});
            skSolve(sketch);
        }
        {
            var Q0;
            Q0 = qSketchRegion(id + "F23", true);
            extrude(context, id + "F24", {"entities" : qUnion([Q0]), "operationType" : NewBodyOperationType.REMOVE, "oppositeDirection" : true, "depth" : 3 * mm, "offsetDistance" : 25 * mm});
        }
        {
            var Q0;
            {var subQ0=sQuery(id+"F0.wireOp",EDGE,"E12.left");var subQ1=sQuery(id+"F0.wireOp",EDGE,"E12.top");var subQ2=sQuery(id+"F0.wireOp",EDGE,"E12.bottom");var subQ3=sQuery(id+"F0.wireOp",EDGE,"E11.left");var subQ4=sQuery(id+"F0.wireOp",EDGE,"E11.top");var subQ5=sQuery(id+"F0.wireOp",EDGE,"E11.bottom");var subQ6=sQuery(id+"F0.wireOp",EDGE,"E7.filletArc");var subQ7=sQuery(id+"F0.wireOp",EDGE,"E6.filletArc");var subQ8=sQuery(id+"F0.wireOp",EDGE,"E5.MirrorCS");var subQ9=sQuery(id+"F0.wireOp",EDGE,"E3.MirrorCS");var subQ10=sQuery(id+"F0.wireOp",EDGE,"E2.MirrorCS");var subQ11=sQuery(id+"F0.wireOp",EDGE,"E19.MirrorCS");var subQ13=sQuery(id+"F0.wireOp",EDGE,"E0.right");var subQ15=sQuery(id+"F0.wireOp",EDGE,"E0.left");var subQ17=sQuery(id+"F0.wireOp",EDGE,"E1.top");var subQ18=sQuery(id+"F0.wireOp",EDGE,"E8.filletArc");var subQ19=sQuery(id+"F0.wireOp",EDGE,"E1.bottom");var subQ20=sQuery(id+"F0.wireOp",EDGE,"E11.right");var subQ21=sQuery(id+"F0.wireOp",EDGE,"E0.bottom");var subQ22=sQuery(id+"F0.wireOp",EDGE,"E10.right");var subQ23=sQuery(id+"F0.wireOp",EDGE,"E1.right");var subQ26=sQuery(id+"F0.wireOp",EDGE,"E13.top");var subQ27=sQuery(id+"F0.wireOp",EDGE,"E9.filletArc");var subQ29=sQuery(id+"F0.wireOp",EDGE,"E13.bottom");var subQ30=sQuery(id+"F0.wireOp",EDGE,"E20.MirrorCS");var subQ31=sQuery(id+"F0.wireOp",EDGE,"E12.right");var subQ32=sQuery(id+"F0.wireOp",EDGE,"E13.right");var subQ33=sQuery(id+"F0.wireOp",EDGE,"E14.MirrorCS");var subQ34=sQuery(id+"F0.wireOp",EDGE,"E15.MirrorCS");var subQ35=sQuery(id+"F0.wireOp",EDGE,"E16.MirrorCS");var subQ36=sQuery(id+"F0.wireOp",EDGE,"E17.MirrorCS");var subQ37=sQuery(id+"F0.wireOp",EDGE,"E21.MirrorCS");var subQ38=sQuery(id+"F0.wireOp",EDGE,"E22.MirrorCS");var subQ39=sQuery(id+"F0.wireOp",EDGE,"E23.MirrorCS");var subQ40=sQuery(id+"F0.wireOp",EDGE,"E24.MirrorCS");var subQ41=sQuery(id+"F0.wireOp",EDGE,"E25.MirrorCS");Q0=makeQuery(id+"F12.boolean.opBoolean","SPLIT",FACE,{"disambiguationData":[TD([makeQuery(id+"F1.opExtrude","SWEPT_FACE",FACE,{"disambiguationData":[OSD([subQ21])]})])],"derivedFrom":makeQuery(id+"F1.opExtrude","CAP_FACE",FACE,{"disambiguationData":[OSD([subQ21,sQuery(id+"F0.wireOp",EDGE,"E0.top"),subQ15,subQ13,subQ19,subQ17,subQ23,subQ10,subQ9,subQ8,subQ7,subQ6,subQ18,subQ27,subQ22,subQ5,subQ4,subQ3,subQ20,subQ2,subQ1,subQ0,subQ31,subQ29,subQ26,subQ32,subQ33,subQ34,subQ35,subQ36,subQ11,subQ30,subQ37,subQ38,subQ39,subQ40,subQ41])],"isStart":false})});}
            var sketch = newSketch(context, id + "F25", { "sketchPlane" : qUnion([Q0])});
            skLineSegment(sketch, "E87.bottom", {"start": v(15, 30) * mm, "end": v(-15, 30) * mm});
            skLineSegment(sketch, "E87.top", {"start": v(15, 0) * mm, "end": v(-15, 0) * mm});
            skLineSegment(sketch, "E87.left", {"start": v(15, 30) * mm, "end": v(15, 0) * mm});
            skLineSegment(sketch, "E87.right", {"start": v(-15, 30) * mm, "end": v(-15, 0) * mm});
            skPoint(sketch, "E87.middle", {"position": v(0, 15) * mm});
            skLineSegment(sketch, "E88", {"start": v(-12.5, 0) * mm, "end": v(15, 27.5) * mm});
            skLineSegment(sketch, "E89", {"start": v(-15, 2.5) * mm, "end": v(12.5, 30) * mm});
            skLineSegment(sketch, "E90", {"start": v(-15, 27.5) * mm, "end": v(12.5, 0) * mm});
            skLineSegment(sketch, "E91", {"start": v(-12.5, 30) * mm, "end": v(15, 2.5) * mm});
            skSolve(sketch);
        }
        {
            var Q0;
            {var subQ0=sQuery(id+"F25.wireOp",EDGE,"E89");var subQ1=sQuery(id+"F25.wireOp",EDGE,"E87.bottom");var subQ2=makeQuery(id+"F25.imprint","INTERSECT",VERTEX,{"derivedFrom":[subQ1,subQ0]});Q0=makeQuery(id+"F25.imprint","IMPRINT",FACE,{"disambiguationData":[TD([[makeQuery(id+"F25.imprint","IMPRINT",EDGE,{"disambiguationData":[TD([[subQ2,-1.0]])],"derivedFrom":subQ1}),1.0]])]});}
            var Q1;
            {var subQ0=sQuery(id+"F25.wireOp",EDGE,"E89");var subQ1=sQuery(id+"F25.wireOp",EDGE,"E87.right");var subQ2=makeQuery(id+"F25.imprint","INTERSECT",VERTEX,{"derivedFrom":[subQ1,subQ0]});Q1=makeQuery(id+"F25.imprint","IMPRINT",FACE,{"disambiguationData":[TD([[makeQuery(id+"F25.imprint","IMPRINT",EDGE,{"disambiguationData":[TD([[subQ2,1.0]])],"derivedFrom":subQ1}),1.0]])]});}
            var Q2;
            {var subQ0=sQuery(id+"F25.wireOp",EDGE,"E88");var subQ1=sQuery(id+"F25.wireOp",EDGE,"E87.top");var subQ2=makeQuery(id+"F25.imprint","INTERSECT",VERTEX,{"derivedFrom":[subQ1,subQ0]});Q2=makeQuery(id+"F25.imprint","IMPRINT",FACE,{"disambiguationData":[TD([[makeQuery(id+"F25.imprint","IMPRINT",EDGE,{"disambiguationData":[TD([[subQ2,1.0]])],"derivedFrom":subQ1}),-1.0]])]});}
            var Q3;
            {var subQ0=sQuery(id+"F25.wireOp",EDGE,"E88");var subQ1=sQuery(id+"F25.wireOp",EDGE,"E87.left");var subQ2=makeQuery(id+"F25.imprint","INTERSECT",VERTEX,{"derivedFrom":[subQ1,subQ0]});Q3=makeQuery(id+"F25.imprint","IMPRINT",FACE,{"disambiguationData":[TD([[makeQuery(id+"F25.imprint","IMPRINT",EDGE,{"disambiguationData":[TD([[subQ2,-1.0]])],"derivedFrom":subQ1}),-1.0]])]});}
            extrude(context, id + "F26", {"entities" : qUnion([Q0, Q1, Q2, Q3]), "operationType" : NewBodyOperationType.REMOVE, "oppositeDirection" : true, "depth" : 25 * mm, "offsetDistance" : 25 * mm});
        }
        {
            var Q0;
            Q0=makeQuery(id+"F12.boolean.opBoolean","COPY",FACE,{"derivedFrom":makeQuery(id+"F12.opExtrude","CAP_FACE",FACE,{"disambiguationData":[OSD([sQuery(id+"F10.wireOp",EDGE,"E53.bottom"),sQuery(id+"F10.wireOp",EDGE,"E53.top"),sQuery(id+"F10.wireOp",EDGE,"E53.left"),sQuery(id+"F10.wireOp",EDGE,"E53.right"),sQuery(id+"F10.wireOp",EDGE,"E54.top"),sQuery(id+"F10.wireOp",EDGE,"E55.MirrorCS")])],"isStart":false})});
            var sketch = newSketch(context, id + "F27", { "sketchPlane" : qUnion([Q0])});
            skLineSegment(sketch, "E92.bottom", {"start": v(-42.5, -46.5) * mm, "end": v(-17.5, -46.5) * mm});
            skLineSegment(sketch, "E92.top", {"start": v(-42.5, -21.5) * mm, "end": v(-17.5, -21.5) * mm});
            skLineSegment(sketch, "E92.left", {"start": v(-42.5, -46.5) * mm, "end": v(-42.5, -21.5) * mm});
            skLineSegment(sketch, "E92.right", {"start": v(-17.5, -46.5) * mm, "end": v(-17.5, -21.5) * mm});
            skLineSegment(sketch, "E93", {"start": v(-42.5, -24) * mm, "end": v(-20, -46.5) * mm});
            skLineSegment(sketch, "E94", {"start": v(-40, -21.5) * mm, "end": v(-17.5, -44) * mm});
            skLineSegment(sketch, "E95", {"start": v(-42.5, -44) * mm, "end": v(-20, -21.5) * mm});
            skLineSegment(sketch, "E96", {"start": v(-40, -46.5) * mm, "end": v(-17.5, -24) * mm});
            skLineSegment(sketch, "E97.1.0.0", {"start": v(-10, -21.5) * mm, "end": v(12.5, -44) * mm});
            skLineSegment(sketch, "E97.1.0.1", {"start": v(-12.5, -44) * mm, "end": v(10, -21.5) * mm});
            skLineSegment(sketch, "E97.1.0.2", {"start": v(12.5, -46.5) * mm, "end": v(12.5, -21.5) * mm});
            skLineSegment(sketch, "E97.1.0.3", {"start": v(-12.5, -24) * mm, "end": v(10, -46.5) * mm});
            skLineSegment(sketch, "E97.1.0.4", {"start": v(-12.5, -46.5) * mm, "end": v(12.5, -46.5) * mm});
            skLineSegment(sketch, "E97.1.0.5", {"start": v(-10, -46.5) * mm, "end": v(12.5, -24) * mm});
            skLineSegment(sketch, "E97.1.0.6", {"start": v(-12.5, -21.5) * mm, "end": v(12.5, -21.5) * mm});
            skLineSegment(sketch, "E97.1.0.7", {"start": v(-12.5, -46.5) * mm, "end": v(-12.5, -21.5) * mm});
            skLineSegment(sketch, "E97.2.0.0", {"start": v(20, -21.5) * mm, "end": v(42.5, -44) * mm});
            skLineSegment(sketch, "E97.2.0.1", {"start": v(17.5, -44) * mm, "end": v(40, -21.5) * mm});
            skLineSegment(sketch, "E97.2.0.2", {"start": v(42.5, -46.5) * mm, "end": v(42.5, -21.5) * mm});
            skLineSegment(sketch, "E97.2.0.3", {"start": v(17.5, -24) * mm, "end": v(40, -46.5) * mm});
            skLineSegment(sketch, "E97.2.0.4", {"start": v(17.5, -46.5) * mm, "end": v(42.5, -46.5) * mm});
            skLineSegment(sketch, "E97.2.0.5", {"start": v(20, -46.5) * mm, "end": v(42.5, -24) * mm});
            skLineSegment(sketch, "E97.2.0.6", {"start": v(17.5, -21.5) * mm, "end": v(42.5, -21.5) * mm});
            skLineSegment(sketch, "E97.2.0.7", {"start": v(17.5, -46.5) * mm, "end": v(17.5, -21.5) * mm});
            skLineSegment(sketch, "E97.direction1", {"start": v(-42.5, -46.5) * mm, "end": v(-12.5, -46.5) * mm, "construction": true});
            skSolve(sketch);
        }
        {
            var Q0;
            {var subQ0=sQuery(id+"F27.wireOp",EDGE,"E93");var subQ1=sQuery(id+"F27.wireOp",EDGE,"E92.bottom");var subQ2=makeQuery(id+"F27.imprint","INTERSECT",VERTEX,{"derivedFrom":[subQ1,subQ0]});Q0=makeQuery(id+"F27.imprint","IMPRINT",FACE,{"disambiguationData":[TD([[makeQuery(id+"F27.imprint","IMPRINT",EDGE,{"disambiguationData":[TD([[subQ2,1.0]])],"derivedFrom":subQ1}),1.0]])]});}
            var Q1;
            {var subQ0=sQuery(id+"F27.wireOp",EDGE,"E94");var subQ1=sQuery(id+"F27.wireOp",EDGE,"E92.top");var subQ2=makeQuery(id+"F27.imprint","INTERSECT",VERTEX,{"derivedFrom":[subQ1,subQ0]});Q1=makeQuery(id+"F27.imprint","IMPRINT",FACE,{"disambiguationData":[TD([[makeQuery(id+"F27.imprint","IMPRINT",EDGE,{"disambiguationData":[TD([[subQ2,-1.0]])],"derivedFrom":subQ1}),-1.0]])]});}
            var Q2;
            {var subQ0=sQuery(id+"F27.wireOp",EDGE,"E93");var subQ1=sQuery(id+"F27.wireOp",EDGE,"E92.left");var subQ2=makeQuery(id+"F27.imprint","INTERSECT",VERTEX,{"derivedFrom":[subQ1,subQ0]});Q2=makeQuery(id+"F27.imprint","IMPRINT",FACE,{"disambiguationData":[TD([[makeQuery(id+"F27.imprint","IMPRINT",EDGE,{"disambiguationData":[TD([[subQ2,1.0]])],"derivedFrom":subQ1}),-1.0]])]});}
            var Q3;
            {var subQ0=sQuery(id+"F27.wireOp",EDGE,"E94");var subQ1=sQuery(id+"F27.wireOp",EDGE,"E92.right");var subQ2=makeQuery(id+"F27.imprint","INTERSECT",VERTEX,{"derivedFrom":[subQ1,subQ0]});Q3=makeQuery(id+"F27.imprint","IMPRINT",FACE,{"disambiguationData":[TD([[makeQuery(id+"F27.imprint","IMPRINT",EDGE,{"disambiguationData":[TD([[subQ2,-1.0]])],"derivedFrom":subQ1}),1.0]])]});}
            var Q4;
            {var subQ0=sQuery(id+"F27.wireOp",EDGE,"E97.1.0.6");var subQ1=sQuery(id+"F27.wireOp",EDGE,"E97.1.0.0");var subQ2=makeQuery(id+"F27.imprint","INTERSECT",VERTEX,{"derivedFrom":[subQ1,subQ0]});Q4=makeQuery(id+"F27.imprint","IMPRINT",FACE,{"disambiguationData":[TD([[makeQuery(id+"F27.imprint","IMPRINT",EDGE,{"disambiguationData":[TD([[subQ2,-1.0]])],"derivedFrom":subQ1}),1.0]])]});}
            var Q5;
            {var subQ0=sQuery(id+"F27.wireOp",EDGE,"E97.1.0.2");var subQ1=sQuery(id+"F27.wireOp",EDGE,"E97.1.0.0");var subQ2=makeQuery(id+"F27.imprint","INTERSECT",VERTEX,{"derivedFrom":[subQ1,subQ0]});Q5=makeQuery(id+"F27.imprint","IMPRINT",FACE,{"disambiguationData":[TD([[makeQuery(id+"F27.imprint","IMPRINT",EDGE,{"disambiguationData":[TD([[subQ2,1.0]])],"derivedFrom":subQ1}),1.0]])]});}
            var Q6;
            {var subQ0=sQuery(id+"F27.wireOp",EDGE,"E97.1.0.7");var subQ1=sQuery(id+"F27.wireOp",EDGE,"E97.1.0.1");var subQ2=makeQuery(id+"F27.imprint","INTERSECT",VERTEX,{"derivedFrom":[subQ1,subQ0]});Q6=makeQuery(id+"F27.imprint","IMPRINT",FACE,{"disambiguationData":[TD([[makeQuery(id+"F27.imprint","IMPRINT",EDGE,{"disambiguationData":[TD([[subQ2,-1.0]])],"derivedFrom":subQ1}),1.0]])]});}
            var Q7;
            {var subQ0=sQuery(id+"F27.wireOp",EDGE,"E97.1.0.4");var subQ1=sQuery(id+"F27.wireOp",EDGE,"E97.1.0.3");var subQ2=makeQuery(id+"F27.imprint","INTERSECT",VERTEX,{"derivedFrom":[subQ1,subQ0]});Q7=makeQuery(id+"F27.imprint","IMPRINT",FACE,{"disambiguationData":[TD([[makeQuery(id+"F27.imprint","IMPRINT",EDGE,{"disambiguationData":[TD([[subQ2,1.0]])],"derivedFrom":subQ1}),-1.0]])]});}
            var Q8;
            {var subQ0=sQuery(id+"F27.wireOp",EDGE,"E97.2.0.6");var subQ1=sQuery(id+"F27.wireOp",EDGE,"E97.2.0.0");var subQ2=makeQuery(id+"F27.imprint","INTERSECT",VERTEX,{"derivedFrom":[subQ1,subQ0]});Q8=makeQuery(id+"F27.imprint","IMPRINT",FACE,{"disambiguationData":[TD([[makeQuery(id+"F27.imprint","IMPRINT",EDGE,{"disambiguationData":[TD([[subQ2,-1.0]])],"derivedFrom":subQ1}),1.0]])]});}
            var Q9;
            {var subQ0=sQuery(id+"F27.wireOp",EDGE,"E97.2.0.2");var subQ1=sQuery(id+"F27.wireOp",EDGE,"E97.2.0.0");var subQ2=makeQuery(id+"F27.imprint","INTERSECT",VERTEX,{"derivedFrom":[subQ1,subQ0]});Q9=makeQuery(id+"F27.imprint","IMPRINT",FACE,{"disambiguationData":[TD([[makeQuery(id+"F27.imprint","IMPRINT",EDGE,{"disambiguationData":[TD([[subQ2,1.0]])],"derivedFrom":subQ1}),1.0]])]});}
            var Q10;
            {var subQ0=sQuery(id+"F27.wireOp",EDGE,"E97.2.0.7");var subQ1=sQuery(id+"F27.wireOp",EDGE,"E97.2.0.1");var subQ2=makeQuery(id+"F27.imprint","INTERSECT",VERTEX,{"derivedFrom":[subQ1,subQ0]});Q10=makeQuery(id+"F27.imprint","IMPRINT",FACE,{"disambiguationData":[TD([[makeQuery(id+"F27.imprint","IMPRINT",EDGE,{"disambiguationData":[TD([[subQ2,-1.0]])],"derivedFrom":subQ1}),1.0]])]});}
            var Q11;
            {var subQ0=sQuery(id+"F27.wireOp",EDGE,"E97.2.0.4");var subQ1=sQuery(id+"F27.wireOp",EDGE,"E97.2.0.3");var subQ2=makeQuery(id+"F27.imprint","INTERSECT",VERTEX,{"derivedFrom":[subQ1,subQ0]});Q11=makeQuery(id+"F27.imprint","IMPRINT",FACE,{"disambiguationData":[TD([[makeQuery(id+"F27.imprint","IMPRINT",EDGE,{"disambiguationData":[TD([[subQ2,1.0]])],"derivedFrom":subQ1}),-1.0]])]});}
            extrude(context, id + "F28", {"entities" : qUnion([Q0, Q1, Q2, Q3, Q4, Q5, Q6, Q7, Q8, Q9, Q10, Q11]), "operationType" : NewBodyOperationType.REMOVE, "oppositeDirection" : true, "depth" : 25 * mm, "offsetDistance" : 25 * mm});
        }
        {
            var Q0;
            Q0=makeQuery(id+"F1.opExtrude","CAP_FACE",FACE,{"disambiguationData":[OSD([sQuery(id+"F0.wireOp",EDGE,"E0.bottom"),sQuery(id+"F0.wireOp",EDGE,"E0.top"),sQuery(id+"F0.wireOp",EDGE,"E0.left"),sQuery(id+"F0.wireOp",EDGE,"E0.right"),sQuery(id+"F0.wireOp",EDGE,"E1.bottom"),sQuery(id+"F0.wireOp",EDGE,"E1.top"),sQuery(id+"F0.wireOp",EDGE,"E1.right"),sQuery(id+"F0.wireOp",EDGE,"E2.MirrorCS"),sQuery(id+"F0.wireOp",EDGE,"E3.MirrorCS"),sQuery(id+"F0.wireOp",EDGE,"E5.MirrorCS"),sQuery(id+"F0.wireOp",EDGE,"E6.filletArc"),sQuery(id+"F0.wireOp",EDGE,"E7.filletArc"),sQuery(id+"F0.wireOp",EDGE,"E8.filletArc"),sQuery(id+"F0.wireOp",EDGE,"E9.filletArc"),sQuery(id+"F0.wireOp",EDGE,"E10.right"),sQuery(id+"F0.wireOp",EDGE,"E11.bottom"),sQuery(id+"F0.wireOp",EDGE,"E11.top"),sQuery(id+"F0.wireOp",EDGE,"E11.left"),sQuery(id+"F0.wireOp",EDGE,"E11.right"),sQuery(id+"F0.wireOp",EDGE,"E12.bottom"),sQuery(id+"F0.wireOp",EDGE,"E12.top"),sQuery(id+"F0.wireOp",EDGE,"E12.left"),sQuery(id+"F0.wireOp",EDGE,"E12.right"),sQuery(id+"F0.wireOp",EDGE,"E13.bottom"),sQuery(id+"F0.wireOp",EDGE,"E13.top"),sQuery(id+"F0.wireOp",EDGE,"E13.right"),sQuery(id+"F0.wireOp",EDGE,"E14.MirrorCS"),sQuery(id+"F0.wireOp",EDGE,"E15.MirrorCS"),sQuery(id+"F0.wireOp",EDGE,"E16.MirrorCS"),sQuery(id+"F0.wireOp",EDGE,"E17.MirrorCS"),sQuery(id+"F0.wireOp",EDGE,"E19.MirrorCS"),sQuery(id+"F0.wireOp",EDGE,"E20.MirrorCS"),sQuery(id+"F0.wireOp",EDGE,"E21.MirrorCS"),sQuery(id+"F0.wireOp",EDGE,"E22.MirrorCS"),sQuery(id+"F0.wireOp",EDGE,"E23.MirrorCS"),sQuery(id+"F0.wireOp",EDGE,"E24.MirrorCS"),sQuery(id+"F0.wireOp",EDGE,"E25.MirrorCS")])],"isStart":true});
            var sketch = newSketch(context, id + "F29", { "sketchPlane" : qUnion([Q0])});
            skLineSegment(sketch, "E98.bottom", {"start": v(-27.6, -105) * mm, "end": v(-22.4, -105) * mm});
            skLineSegment(sketch, "E98.top", {"start": v(-27.6, -88.25) * mm, "end": v(-22.4, -88.25) * mm});
            skLineSegment(sketch, "E98.left", {"start": v(-27.6, -105) * mm, "end": v(-27.6, -88.25) * mm});
            skLineSegment(sketch, "E98.right", {"start": v(-22.4, -105) * mm, "end": v(-22.4, -88.25) * mm});
            skLineSegment(sketch, "E99.MirrorCS", {"start": v(27.6, -105) * mm, "end": v(22.4, -105) * mm});
            skLineSegment(sketch, "E100.MirrorCS", {"start": v(27.6, -88.25) * mm, "end": v(22.4, -88.25) * mm});
            skLineSegment(sketch, "E101.MirrorCS", {"start": v(22.4, -105) * mm, "end": v(22.4, -88.25) * mm});
            skLineSegment(sketch, "E102.MirrorCS", {"start": v(27.6, -105) * mm, "end": v(27.6, -88.25) * mm});
            skSolve(sketch);
        }
        {
            var Q0;
            Q0 = qSketchRegion(id + "F29", true);
            extrude(context, id + "F30", {"entities" : qUnion([Q0]), "operationType" : NewBodyOperationType.REMOVE, "oppositeDirection" : true, "depth" : 2 * mm, "offsetDistance" : 25 * mm});
        }
        {
            var Q0;
            Q0=makeQuery(id+"F1.opExtrude","CAP_FACE",FACE,{"disambiguationData":[OSD([sQuery(id+"F0.wireOp",EDGE,"E0.bottom"),sQuery(id+"F0.wireOp",EDGE,"E0.top"),sQuery(id+"F0.wireOp",EDGE,"E0.left"),sQuery(id+"F0.wireOp",EDGE,"E0.right"),sQuery(id+"F0.wireOp",EDGE,"E1.bottom"),sQuery(id+"F0.wireOp",EDGE,"E1.top"),sQuery(id+"F0.wireOp",EDGE,"E1.right"),sQuery(id+"F0.wireOp",EDGE,"E2.MirrorCS"),sQuery(id+"F0.wireOp",EDGE,"E3.MirrorCS"),sQuery(id+"F0.wireOp",EDGE,"E5.MirrorCS"),sQuery(id+"F0.wireOp",EDGE,"E6.filletArc"),sQuery(id+"F0.wireOp",EDGE,"E7.filletArc"),sQuery(id+"F0.wireOp",EDGE,"E8.filletArc"),sQuery(id+"F0.wireOp",EDGE,"E9.filletArc"),sQuery(id+"F0.wireOp",EDGE,"E10.right"),sQuery(id+"F0.wireOp",EDGE,"E11.bottom"),sQuery(id+"F0.wireOp",EDGE,"E11.top"),sQuery(id+"F0.wireOp",EDGE,"E11.left"),sQuery(id+"F0.wireOp",EDGE,"E11.right"),sQuery(id+"F0.wireOp",EDGE,"E12.bottom"),sQuery(id+"F0.wireOp",EDGE,"E12.top"),sQuery(id+"F0.wireOp",EDGE,"E12.left"),sQuery(id+"F0.wireOp",EDGE,"E12.right"),sQuery(id+"F0.wireOp",EDGE,"E13.bottom"),sQuery(id+"F0.wireOp",EDGE,"E13.top"),sQuery(id+"F0.wireOp",EDGE,"E13.right"),sQuery(id+"F0.wireOp",EDGE,"E14.MirrorCS"),sQuery(id+"F0.wireOp",EDGE,"E15.MirrorCS"),sQuery(id+"F0.wireOp",EDGE,"E16.MirrorCS"),sQuery(id+"F0.wireOp",EDGE,"E17.MirrorCS"),sQuery(id+"F0.wireOp",EDGE,"E19.MirrorCS"),sQuery(id+"F0.wireOp",EDGE,"E20.MirrorCS"),sQuery(id+"F0.wireOp",EDGE,"E21.MirrorCS"),sQuery(id+"F0.wireOp",EDGE,"E22.MirrorCS"),sQuery(id+"F0.wireOp",EDGE,"E23.MirrorCS"),sQuery(id+"F0.wireOp",EDGE,"E24.MirrorCS"),sQuery(id+"F0.wireOp",EDGE,"E25.MirrorCS")])],"isStart":true});
            var sketch = newSketch(context, id + "F31", { "sketchPlane" : qUnion([Q0])});
            skCircle(sketch, "E103", {"center": v(19.25, 65) * mm, "radius": 1.75 * mm});
            skCircle(sketch, "E104.MirrorC", {"center": v(-19.25, 65) * mm, "radius": 1.75 * mm});
            skSolve(sketch);
        }
        {
            var Q0;
            Q0=makeQuery(id+"F31.imprint","IMPRINT",FACE,{"disambiguationData":[TD([[makeQuery(id+"F31.imprint","IMPRINT",EDGE,{"derivedFrom":sQuery(id+"F31.wireOp",EDGE,"E104.MirrorC")}),-1.0]])]});
            var Q1;
            Q1=makeQuery(id+"F31.imprint","IMPRINT",FACE,{"disambiguationData":[TD([[makeQuery(id+"F31.imprint","IMPRINT",EDGE,{"derivedFrom":sQuery(id+"F31.wireOp",EDGE,"E103")}),1.0]])]});
            extrude(context, id + "F32", {"entities" : qUnion([Q0, Q1]), "operationType" : NewBodyOperationType.REMOVE, "oppositeDirection" : true, "depth" : 25 * mm, "offsetDistance" : 25 * mm});
        }
        {
            var Q0;
            {var subQ0=sQuery(id+"F0.wireOp",EDGE,"E9.filletArc");var subQ1=sQuery(id+"F0.wireOp",EDGE,"E0.right");var subQ2=sQuery(id+"F0.wireOp",EDGE,"E5.MirrorCS");var subQ3=sQuery(id+"F0.wireOp",EDGE,"E8.filletArc");var subQ4=sQuery(id+"F0.wireOp",EDGE,"E0.left");var subQ5=sQuery(id+"F0.wireOp",EDGE,"E1.bottom");var subQ6=sQuery(id+"F0.wireOp",EDGE,"E0.top");Q0=makeQuery(id+"F12.boolean.opBoolean","SPLIT",FACE,{"disambiguationData":[TD([makeQuery(id+"F1.opExtrude","SWEPT_FACE",FACE,{"disambiguationData":[OSD([subQ6])]})])],"derivedFrom":makeQuery(id+"F1.opExtrude","CAP_FACE",FACE,{"disambiguationData":[OSD([sQuery(id+"F0.wireOp",EDGE,"E0.bottom"),subQ6,subQ4,subQ1,subQ5,sQuery(id+"F0.wireOp",EDGE,"E1.top"),sQuery(id+"F0.wireOp",EDGE,"E1.right"),sQuery(id+"F0.wireOp",EDGE,"E2.MirrorCS"),sQuery(id+"F0.wireOp",EDGE,"E3.MirrorCS"),subQ2,sQuery(id+"F0.wireOp",EDGE,"E6.filletArc"),sQuery(id+"F0.wireOp",EDGE,"E7.filletArc"),subQ3,subQ0,sQuery(id+"F0.wireOp",EDGE,"E10.right"),sQuery(id+"F0.wireOp",EDGE,"E11.bottom"),sQuery(id+"F0.wireOp",EDGE,"E11.top"),sQuery(id+"F0.wireOp",EDGE,"E11.left"),sQuery(id+"F0.wireOp",EDGE,"E11.right"),sQuery(id+"F0.wireOp",EDGE,"E12.bottom"),sQuery(id+"F0.wireOp",EDGE,"E12.top"),sQuery(id+"F0.wireOp",EDGE,"E12.left"),sQuery(id+"F0.wireOp",EDGE,"E12.right"),sQuery(id+"F0.wireOp",EDGE,"E13.bottom"),sQuery(id+"F0.wireOp",EDGE,"E13.top"),sQuery(id+"F0.wireOp",EDGE,"E13.right"),sQuery(id+"F0.wireOp",EDGE,"E14.MirrorCS"),sQuery(id+"F0.wireOp",EDGE,"E15.MirrorCS"),sQuery(id+"F0.wireOp",EDGE,"E16.MirrorCS"),sQuery(id+"F0.wireOp",EDGE,"E17.MirrorCS"),sQuery(id+"F0.wireOp",EDGE,"E19.MirrorCS"),sQuery(id+"F0.wireOp",EDGE,"E20.MirrorCS"),sQuery(id+"F0.wireOp",EDGE,"E21.MirrorCS"),sQuery(id+"F0.wireOp",EDGE,"E22.MirrorCS"),sQuery(id+"F0.wireOp",EDGE,"E23.MirrorCS"),sQuery(id+"F0.wireOp",EDGE,"E24.MirrorCS"),sQuery(id+"F0.wireOp",EDGE,"E25.MirrorCS")])],"isStart":false})});}
            var sketch = newSketch(context, id + "F33", { "sketchPlane" : qUnion([Q0])});
            skCircle(sketch, "E105.cCircle", {"center": v(-19.25, -65) * mm, "radius": 3.1 * mm, "construction": true});
            skLineSegment(sketch, "E105.0", {"start": v(-21.04, -61.9) * mm, "end": v(-17.46, -61.9) * mm});
            skLineSegment(sketch, "E105.1", {"start": v(-17.46, -61.9) * mm, "end": v(-15.67, -65) * mm});
            skLineSegment(sketch, "E105.2", {"start": v(-15.67, -65) * mm, "end": v(-17.46, -68.1) * mm});
            skLineSegment(sketch, "E105.3", {"start": v(-17.46, -68.1) * mm, "end": v(-21.04, -68.1) * mm});
            skLineSegment(sketch, "E105.4", {"start": v(-21.04, -68.1) * mm, "end": v(-22.83, -65) * mm});
            skLineSegment(sketch, "E105.5", {"start": v(-22.83, -65) * mm, "end": v(-21.04, -61.9) * mm});
            skPoint(sketch, "E105.0.midPoint", {"position": v(-19.25, -61.9) * mm});
            skLineSegment(sketch, "E106.MirrorCS", {"start": v(15.67, -65) * mm, "end": v(17.46, -68.1) * mm});
            skPoint(sketch, "E107.MirrorP", {"position": v(19.25, -61.9) * mm});
            skLineSegment(sketch, "E108.MirrorCS", {"start": v(22.83, -65) * mm, "end": v(21.04, -61.9) * mm});
            skLineSegment(sketch, "E109.MirrorCS", {"start": v(17.46, -68.1) * mm, "end": v(21.04, -68.1) * mm});
            skLineSegment(sketch, "E110.MirrorCS", {"start": v(17.46, -61.9) * mm, "end": v(15.67, -65) * mm});
            skLineSegment(sketch, "E111.MirrorCS", {"start": v(21.04, -61.9) * mm, "end": v(17.46, -61.9) * mm});
            skLineSegment(sketch, "E112.MirrorCS", {"start": v(21.04, -68.1) * mm, "end": v(22.83, -65) * mm});
            skCircle(sketch, "E113.MirrorC", {"center": v(19.25, -65) * mm, "radius": 3.1 * mm, "construction": true});
            skSolve(sketch);
        }
        {
            var Q0;
            Q0=makeQuery(id+"F33.imprint","IMPRINT",FACE,{"disambiguationData":[TD([[makeQuery(id+"F33.imprint","IMPRINT",EDGE,{"derivedFrom":sQuery(id+"F33.wireOp",EDGE,"E105.0")}),-1.0]])]});
            var Q1;
            Q1=makeQuery(id+"F33.imprint","IMPRINT",FACE,{"disambiguationData":[TD([[makeQuery(id+"F33.imprint","IMPRINT",EDGE,{"derivedFrom":sQuery(id+"F33.wireOp",EDGE,"E106.MirrorCS")}),1.0]])]});
            extrude(context, id + "F34", {"entities" : qUnion([Q0, Q1]), "operationType" : NewBodyOperationType.REMOVE, "oppositeDirection" : true, "depth" : 3 * mm, "offsetDistance" : 25 * mm});
        }
    });
